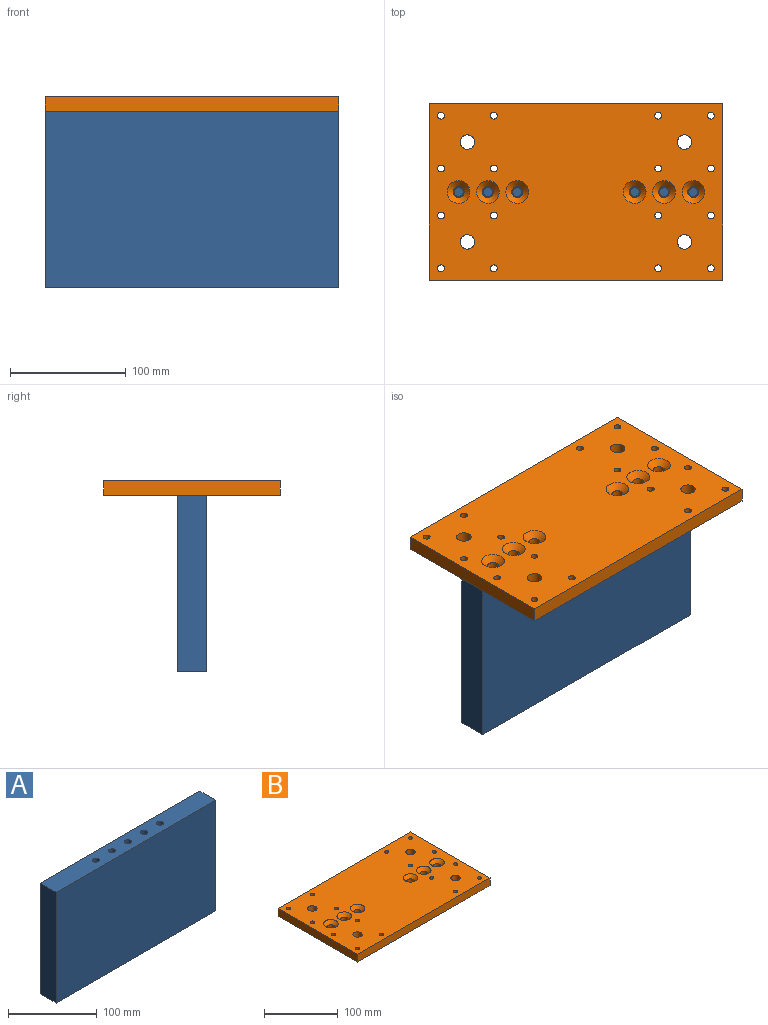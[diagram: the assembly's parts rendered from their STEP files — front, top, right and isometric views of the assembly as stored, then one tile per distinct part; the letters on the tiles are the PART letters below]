
ASSEMBLY  parts=2 mates=1
PART A: 28 faces, bbox 254x25.4x152.4 mm
  f0: plane 152.4x25.4mm, normal (1,0,0), area 3871mm2, adj f1,f3,f4,f5
  f1: plane 254x152.4mm, normal (0,1,0), area 38709.6mm2, adj f0,f2,f4,f5
  f2: plane 152.4x25.4mm, normal (-1,0,0), area 3871mm2, adj f1,f3,f4,f5
  f3: plane 254x152.4mm, normal (0,-1,0), area 38709.6mm2, adj f0,f2,f4,f5
  f4: plane 254x25.4mm, normal (0,0,1), area 6211.3mm2, adj f0,f1,f2,f3,f6,f8,f10,f12
  f5: plane 254x25.4mm, normal (0,0,-1), area 6163.2mm2, adj f0,f1,f2,f3,f16,f18,f20,f22
  f6: cylinder r=3.91mm len=34.16mm, axis (0,0,1), area 839.6mm2, adj f4,f7
  f7: plane 7.82x7.82mm, normal (0,0,1), area 48.1mm2, adj f6
  f8: cylinder r=3.91mm len=34.16mm, axis (0,0,1), area 839.6mm2, adj f4,f9
  f9: plane 7.82x7.82mm, normal (0,0,1), area 48.1mm2, adj f8
  f10: cylinder r=3.91mm len=34.16mm, axis (0,0,1), area 839.6mm2, adj f4,f11
  f11: plane 7.82x7.82mm, normal (0,0,1), area 48.1mm2, adj f10
  f12: cylinder r=3.91mm len=34.16mm, axis (0,0,1), area 839.6mm2, adj f4,f13
  f13: plane 7.82x7.82mm, normal (0,0,1), area 48.1mm2, adj f12
  f14: cylinder r=3.91mm len=34.16mm, axis (0,0,1), area 839.6mm2, adj f4,f15
  f15: plane 7.82x7.82mm, normal (0,0,1), area 48.1mm2, adj f14
  f16: cylinder r=3.91mm len=33.02mm, axis (0,0,-1), area 811.5mm2, adj f5,f17
  f17: plane 7.82x7.82mm, normal (0,0,-1), area 48.1mm2, adj f16
  f18: cylinder r=3.91mm len=33.02mm, axis (0,0,-1), area 811.5mm2, adj f5,f19
  f19: plane 7.82x7.82mm, normal (0,0,-1), area 48.1mm2, adj f18
  f20: cylinder r=3.91mm len=33.02mm, axis (0,0,-1), area 811.5mm2, adj f5,f21
  f21: plane 7.82x7.82mm, normal (0,0,-1), area 48.1mm2, adj f20
  f22: cylinder r=3.91mm len=33.02mm, axis (0,0,-1), area 811.5mm2, adj f5,f23
  f23: plane 7.82x7.82mm, normal (0,0,-1), area 48.1mm2, adj f22
  f24: cylinder r=3.91mm len=33.02mm, axis (0,0,-1), area 811.5mm2, adj f5,f25
  f25: plane 7.82x7.82mm, normal (0,0,-1), area 48.1mm2, adj f24
  f26: cylinder r=3.91mm len=33.02mm, axis (0,0,-1), area 811.5mm2, adj f5,f27
  f27: plane 7.82x7.82mm, normal (0,0,-1), area 48.1mm2, adj f26
PART B: 70 faces, bbox 254x152.4x12.7 mm
  f0: cylinder r=2.95mm len=5.89mm, axis (0,0,1), area 94mm2, adj f20,f68
  f1: cylinder r=2.95mm len=5.89mm, axis (0,0,1), area 94mm2, adj f20,f66
  f2: cylinder r=2.95mm len=5.89mm, axis (0,0,1), area 94mm2, adj f20,f64
  f3: cylinder r=2.95mm len=5.89mm, axis (0,0,1), area 94mm2, adj f20,f62
  f4: cylinder r=2.95mm len=5.89mm, axis (0,0,1), area 94mm2, adj f20,f60
  f5: cylinder r=2.95mm len=5.89mm, axis (0,0,1), area 94mm2, adj f20,f58
  f6: cylinder r=2.95mm len=5.89mm, axis (0,0,1), area 94mm2, adj f20,f56
  f7: cylinder r=2.95mm len=5.89mm, axis (0,0,1), area 94mm2, adj f20,f54
  f8: cylinder r=2.95mm len=5.89mm, axis (0,0,1), area 94mm2, adj f20,f52
  f9: cylinder r=2.95mm len=5.89mm, axis (0,0,1), area 94mm2, adj f20,f50
  f10: cylinder r=2.95mm len=5.89mm, axis (0,0,1), area 94mm2, adj f20,f48
  f11: cylinder r=2.95mm len=5.89mm, axis (0,0,1), area 94mm2, adj f20,f46
  f12: cylinder r=2.95mm len=5.89mm, axis (0,0,1), area 94mm2, adj f20,f44
  f13: cylinder r=2.95mm len=5.89mm, axis (0,0,1), area 94mm2, adj f20,f42
  f14: cylinder r=2.95mm len=5.89mm, axis (0,0,1), area 94mm2, adj f20,f40
  f15: cylinder r=2.95mm len=5.89mm, axis (0,0,1), area 94mm2, adj f20,f38
  f16: plane 152.4x12.7mm, normal (1,0,0), area 1935.5mm2, adj f17,f19,f20,f21
  f17: plane 254x12.7mm, normal (0,1,0), area 3225.8mm2, adj f16,f18,f20,f21
  f18: plane 152.4x12.7mm, normal (-1,0,0), area 1935.5mm2, adj f17,f19,f20,f21
  f19: plane 254x12.7mm, normal (0,-1,0), area 3225.8mm2, adj f16,f18,f20,f21
  f20: plane 254x152.4mm, normal (0,0,1), area 35954.6mm2, adj f0,f1,f2,f3,f4,f5,f6,f7
  f21: plane 254x152.4mm, normal (0,0,-1), area 35762.6mm2, adj f16,f17,f18,f19,f22,f23,f24,f25
  f22: cylinder r=6.26mm len=12.7mm, axis (0,0,1), area 499.6mm2, adj f20,f21
  f23: cylinder r=6.26mm len=12.7mm, axis (0,0,1), area 499.6mm2, adj f20,f21
  f24: cylinder r=6.26mm len=12.7mm, axis (0,0,1), area 499.6mm2, adj f20,f21
  f25: cylinder r=6.26mm len=12.7mm, axis (0,0,1), area 499.6mm2, adj f20,f21
  f26: cylinder r=4.76mm len=9.53mm, axis (0,0,1), area 228mm2, adj f21,f32
  f27: cylinder r=4.76mm len=9.53mm, axis (0,0,1), area 228mm2, adj f21,f33
  f28: cylinder r=4.76mm len=9.53mm, axis (0,0,1), area 228mm2, adj f21,f34
  f29: cylinder r=4.76mm len=9.53mm, axis (0,0,1), area 228mm2, adj f21,f35
  f30: cylinder r=4.76mm len=9.53mm, axis (0,0,1), area 228mm2, adj f21,f36
  f31: cylinder r=4.76mm len=9.53mm, axis (0,0,1), area 228mm2, adj f21,f37
  f32: cone r=4.76mm half-angle=45deg, axis (0,0,1), area 329.6mm2, adj f20,f26
  f33: cone r=4.76mm half-angle=45deg, axis (0,0,1), area 329.6mm2, adj f20,f27
  f34: cone r=4.76mm half-angle=45deg, axis (0,0,1), area 329.6mm2, adj f20,f28
  f35: cone r=4.76mm half-angle=45deg, axis (0,0,1), area 329.6mm2, adj f20,f29
  f36: cone r=4.76mm half-angle=45deg, axis (0,0,1), area 329.6mm2, adj f20,f30
  f37: cone r=4.76mm half-angle=45deg, axis (0,0,1), area 329.6mm2, adj f20,f31
  f38: plane 12.7x12.7mm, normal (0,0,-1), area 99.4mm2, adj f15,f39
  f39: cylinder r=6.35mm len=12.7mm, axis (0,0,-1), area 304mm2, adj f21,f38
  f40: plane 12.7x12.7mm, normal (0,0,-1), area 99.4mm2, adj f14,f41
  f41: cylinder r=6.35mm len=12.7mm, axis (0,0,-1), area 304mm2, adj f21,f40
  f42: plane 12.7x12.7mm, normal (0,0,-1), area 99.4mm2, adj f13,f43
  f43: cylinder r=6.35mm len=12.7mm, axis (0,0,-1), area 304mm2, adj f21,f42
  f44: plane 12.7x12.7mm, normal (0,0,-1), area 99.4mm2, adj f12,f45
  f45: cylinder r=6.35mm len=12.7mm, axis (0,0,-1), area 304mm2, adj f21,f44
  f46: plane 12.7x12.7mm, normal (0,0,-1), area 99.4mm2, adj f11,f47
  f47: cylinder r=6.35mm len=12.7mm, axis (0,0,-1), area 304mm2, adj f21,f46
  f48: plane 12.7x12.7mm, normal (0,0,-1), area 99.4mm2, adj f10,f49
  f49: cylinder r=6.35mm len=12.7mm, axis (0,0,-1), area 304mm2, adj f21,f48
  f50: plane 12.7x12.7mm, normal (0,0,-1), area 99.4mm2, adj f9,f51
  f51: cylinder r=6.35mm len=12.7mm, axis (0,0,-1), area 304mm2, adj f21,f50
  f52: plane 12.7x12.7mm, normal (0,0,-1), area 99.4mm2, adj f8,f53
  f53: cylinder r=6.35mm len=12.7mm, axis (0,0,-1), area 304mm2, adj f21,f52
  f54: plane 12.7x12.7mm, normal (0,0,-1), area 99.4mm2, adj f7,f55
  f55: cylinder r=6.35mm len=12.7mm, axis (0,0,-1), area 304mm2, adj f21,f54
  f56: plane 12.7x12.7mm, normal (0,0,-1), area 99.4mm2, adj f6,f57
  f57: cylinder r=6.35mm len=12.7mm, axis (0,0,-1), area 304mm2, adj f21,f56
  f58: plane 12.7x12.7mm, normal (0,0,-1), area 99.4mm2, adj f5,f59
  f59: cylinder r=6.35mm len=12.7mm, axis (0,0,-1), area 304mm2, adj f21,f58
  f60: plane 12.7x12.7mm, normal (0,0,-1), area 99.4mm2, adj f4,f61
  f61: cylinder r=6.35mm len=12.7mm, axis (0,0,-1), area 304mm2, adj f21,f60
  f62: plane 12.7x12.7mm, normal (0,0,-1), area 99.4mm2, adj f3,f63
  f63: cylinder r=6.35mm len=12.7mm, axis (0,0,-1), area 304mm2, adj f21,f62
  f64: plane 12.7x12.7mm, normal (0,0,-1), area 99.4mm2, adj f2,f65
  f65: cylinder r=6.35mm len=12.7mm, axis (0,0,-1), area 304mm2, adj f21,f64
  f66: plane 12.7x12.7mm, normal (0,0,-1), area 99.4mm2, adj f1,f67
  f67: cylinder r=6.35mm len=12.7mm, axis (0,0,-1), area 304mm2, adj f21,f66
  f68: plane 12.7x12.7mm, normal (0,0,-1), area 99.4mm2, adj f0,f69
  f69: cylinder r=6.35mm len=12.7mm, axis (0,0,-1), area 304mm2, adj f21,f68
PLACE A rot(axis=(1,0,0),180deg) t=(0,0,0)mm
PLACE B at identity
MATE fastened A.f20 <-> B.f28  axis (0,0,1) through (50.8,0,0)mm
